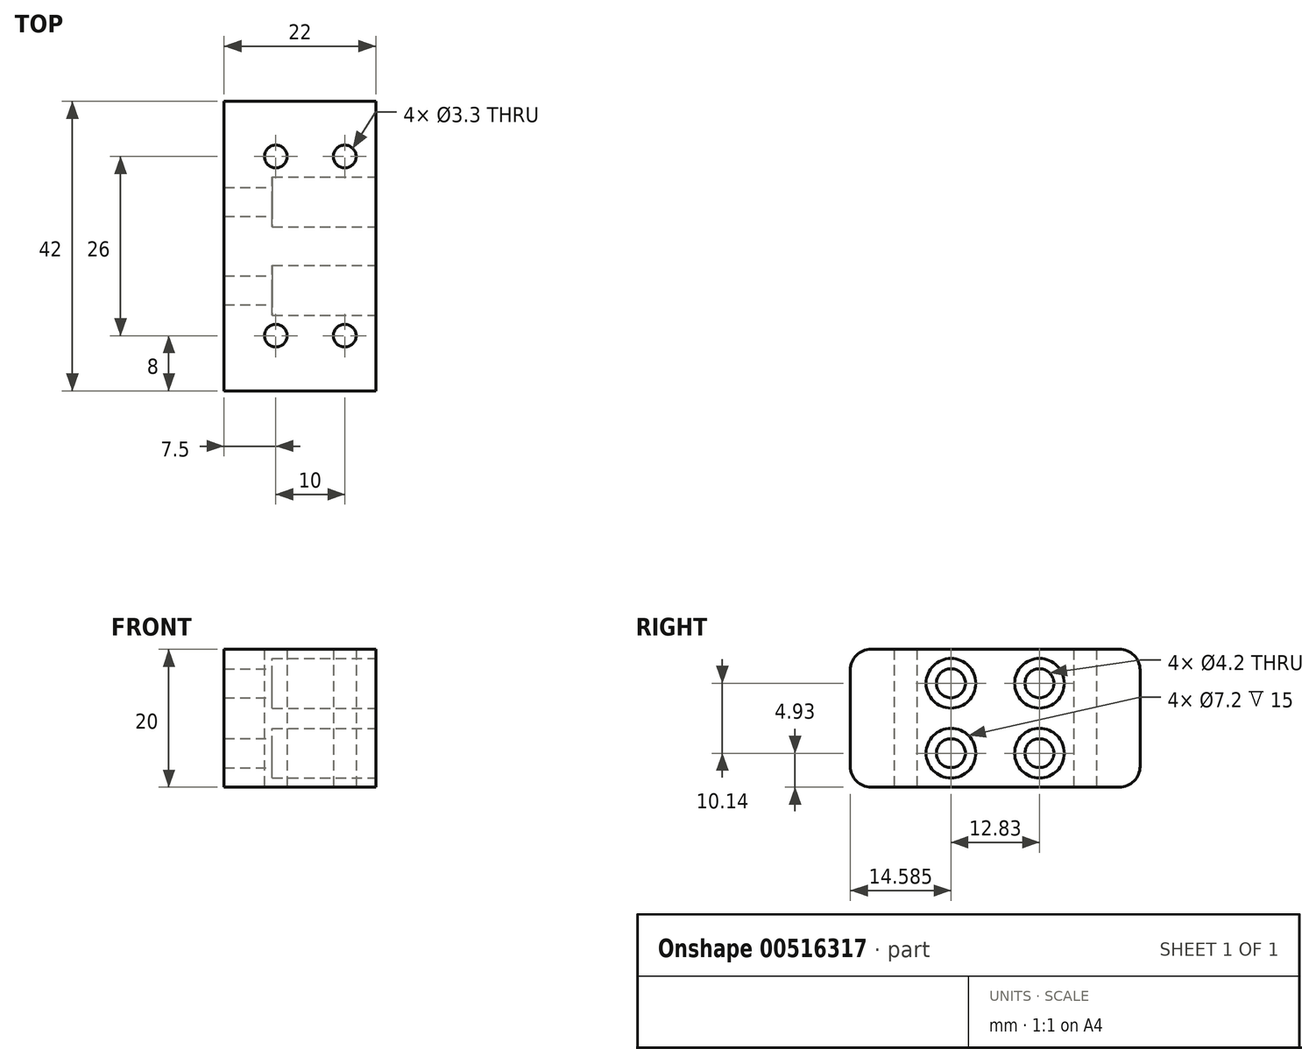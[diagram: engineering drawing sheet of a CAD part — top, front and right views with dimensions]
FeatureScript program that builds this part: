
annotation { "Feature Type Name" : "Feature", "Feature Type Description" : "" }
export const myFeature = defineFeature(function(context is Context, id is Id, definition is map)
    precondition{}
    {
        {
            var Q0;
            Q0=qCreatedBy(makeId("Top.planeOp"),FACE);
            var sketch = newSketch(context, id + "F0", { "sketchPlane" : qUnion([Q0])});
            skCircle(sketch, "E0", {"center": v(-5, -13) * mm, "radius": 1.65 * mm});
            skCircle(sketch, "E1.0.1.0", {"center": v(-5, 13) * mm, "radius": 1.65 * mm});
            skCircle(sketch, "E1.1.0.0", {"center": v(5, -13) * mm, "radius": 1.65 * mm});
            skCircle(sketch, "E1.1.1.0", {"center": v(5, 13) * mm, "radius": 1.65 * mm});
            skLineSegment(sketch, "E1.direction1", {"start": v(-5, -13) * mm, "end": v(5, -13) * mm, "construction": true});
            skLineSegment(sketch, "E1.direction2", {"start": v(-5, -13) * mm, "end": v(-5, 13) * mm, "construction": true});
            skLineSegment(sketch, "E2", {"start": v(5, 13) * mm, "end": v(-5, -13) * mm, "construction": true});
            skLineSegment(sketch, "E3.bottom", {"start": v(-9.5, -21) * mm, "end": v(9.5, -21) * mm});
            skLineSegment(sketch, "E3.top", {"start": v(-9.5, 21) * mm, "end": v(9.5, 21) * mm});
            skLineSegment(sketch, "E3.left", {"start": v(-9.5, -21) * mm, "end": v(-9.5, 21) * mm});
            skLineSegment(sketch, "E3.right", {"start": v(9.5, -21) * mm, "end": v(9.5, 21) * mm});
            skPoint(sketch, "E3.middle", {"position": v(0, 0) * mm});
            skSolve(sketch);
        }
        {
            var Q0;
            Q0=makeQuery(id+"F0.imprint","IMPRINT",FACE,{"disambiguationData":[TD([[makeQuery(id+"F0.imprint","IMPRINT",EDGE,{"derivedFrom":sQuery(id+"F0.wireOp",EDGE,"E0")}),-1.0]])]});
            extrude(context, id + "F1", {"entities" : qUnion([Q0]), "depth" : 20 * mm, "offsetDistance" : 25 * mm});
        }
        {
            var Q0;
            Q0=makeQuery(id+"F1.opExtrude","SWEPT_FACE",FACE,{"disambiguationData":[OSD([sQuery(id+"F0.wireOp",EDGE,"E3.right")])]});
            var sketch = newSketch(context, id + "F2", { "sketchPlane" : qUnion([Q0])});
            skCircle(sketch, "E4", {"center": v(6.41, 4.93) * mm, "radius": 2.1 * mm});
            skCircle(sketch, "E5.0.1.0", {"center": v(6.41, 15.07) * mm, "radius": 2.1 * mm});
            skCircle(sketch, "E5.1.0.0", {"center": v(-6.42, 4.93) * mm, "radius": 2.1 * mm});
            skCircle(sketch, "E5.1.1.0", {"center": v(-6.42, 15.07) * mm, "radius": 2.1 * mm});
            skLineSegment(sketch, "E6", {"start": v(-6.42, 4.93) * mm, "end": v(6.42, 15.07) * mm, "construction": true});
            skLineSegment(sketch, "E7", {"start": v(21, 20) * mm, "end": v(-21, 0) * mm, "construction": true});
            skPoint(sketch, "E8", {"position": v(0, 10) * mm});
            skCircle(sketch, "E9", {"center": v(6.41, 4.93) * mm, "radius": 3.6 * mm});
            skCircle(sketch, "E10.0.1.0", {"center": v(6.42, 15.07) * mm, "radius": 3.6 * mm});
            skCircle(sketch, "E10.1.0.0", {"center": v(-6.41, 4.93) * mm, "radius": 3.6 * mm});
            skCircle(sketch, "E10.1.1.0", {"center": v(-6.41, 15.07) * mm, "radius": 3.6 * mm});
            skLineSegment(sketch, "E10.direction1", {"start": v(6.41, 4.93) * mm, "end": v(-6.41, 4.93) * mm, "construction": true});
            skLineSegment(sketch, "E10.direction2", {"start": v(6.42, 4.93) * mm, "end": v(6.42, 15.07) * mm, "construction": true});
            skSolve(sketch);
        }
        {
            var Q0;
            Q0=makeQuery(id+"F1.opExtrude","SWEPT_FACE",FACE,{"disambiguationData":[OSD([sQuery(id+"F0.wireOp",EDGE,"E3.left")])]});
            extrude(context, id + "F3", {"entities" : qUnion([Q0]), "operationType" : NewBodyOperationType.ADD, "depth" : 3 * mm, "offsetDistance" : 25 * mm});
        }
        {
            var Q0;
            Q0=makeQuery(id+"F2.imprint","IMPRINT",FACE,{"disambiguationData":[TD([[makeQuery(id+"F2.imprint","IMPRINT",EDGE,{"derivedFrom":sQuery(id+"F2.wireOp",EDGE,"E5.1.1.0")}),1.0]])]});
            var Q1;
            Q1=makeQuery(id+"F2.imprint","IMPRINT",FACE,{"disambiguationData":[TD([[makeQuery(id+"F2.imprint","IMPRINT",EDGE,{"derivedFrom":sQuery(id+"F2.wireOp",EDGE,"E5.0.1.0")}),1.0]])]});
            var Q2;
            Q2=makeQuery(id+"F2.imprint","IMPRINT",FACE,{"disambiguationData":[TD([[makeQuery(id+"F2.imprint","IMPRINT",EDGE,{"derivedFrom":sQuery(id+"F2.wireOp",EDGE,"E4")}),1.0]])]});
            var Q3;
            Q3=makeQuery(id+"F2.imprint","IMPRINT",FACE,{"disambiguationData":[TD([[makeQuery(id+"F2.imprint","IMPRINT",EDGE,{"derivedFrom":sQuery(id+"F2.wireOp",EDGE,"E5.1.0.0")}),1.0]])]});
            extrude(context, id + "F4", {"entities" : qUnion([Q0, Q1, Q2, Q3]), "operationType" : NewBodyOperationType.REMOVE, "endBound" : BoundingType.UP_TO_NEXT, "oppositeDirection" : true, "depth" : 25 * mm, "offsetDistance" : 25 * mm});
        }
        {
            var Q0;
            Q0=makeQuery(id+"F2.imprint","IMPRINT",FACE,{"disambiguationData":[TD([[makeQuery(id+"F2.imprint","IMPRINT",EDGE,{"derivedFrom":sQuery(id+"F2.wireOp",EDGE,"E5.0.1.0")}),-1.0]])]});
            var Q1;
            Q1=makeQuery(id+"F2.imprint","IMPRINT",FACE,{"disambiguationData":[TD([[makeQuery(id+"F2.imprint","IMPRINT",EDGE,{"derivedFrom":sQuery(id+"F2.wireOp",EDGE,"E4")}),-1.0]])]});
            var Q2;
            Q2=makeQuery(id+"F2.imprint","IMPRINT",FACE,{"disambiguationData":[TD([[makeQuery(id+"F2.imprint","IMPRINT",EDGE,{"derivedFrom":sQuery(id+"F2.wireOp",EDGE,"E5.1.0.0")}),-1.0]])]});
            var Q3;
            Q3=makeQuery(id+"F2.imprint","IMPRINT",FACE,{"disambiguationData":[TD([[makeQuery(id+"F2.imprint","IMPRINT",EDGE,{"derivedFrom":sQuery(id+"F2.wireOp",EDGE,"E5.1.1.0")}),-1.0]])]});
            extrude(context, id + "F5", {"entities" : qUnion([Q0, Q1, Q2, Q3]), "operationType" : NewBodyOperationType.REMOVE, "oppositeDirection" : true, "depth" : (22 - 7) * mm, "offsetDistance" : 25 * mm});
        }
        {
            var Q0;
            Q0=makeQuery(id+"F1.opExtrude","CAP_EDGE",EDGE,{"disambiguationData":[OSD([sQuery(id+"F0.wireOp",EDGE,"E3.top")])],"isStart":true});
            var Q1;
            Q1=makeQuery(id+"F1.opExtrude","CAP_EDGE",EDGE,{"disambiguationData":[OSD([sQuery(id+"F0.wireOp",EDGE,"E3.bottom")])],"isStart":true});
            var Q2;
            Q2=makeQuery(id+"F1.opExtrude","CAP_EDGE",EDGE,{"disambiguationData":[OSD([sQuery(id+"F0.wireOp",EDGE,"E3.bottom")])],"isStart":false});
            var Q3;
            Q3=makeQuery(id+"F1.opExtrude","CAP_EDGE",EDGE,{"disambiguationData":[OSD([sQuery(id+"F0.wireOp",EDGE,"E3.top")])],"isStart":false});
            fillet(context, id + "F6", {"entities" : qUnion([Q0, Q1, Q2, Q3]), "radius" : 3 * mm, "tangentPropagation" : true, "allowEdgeOverflow" : false});
        }
    });
